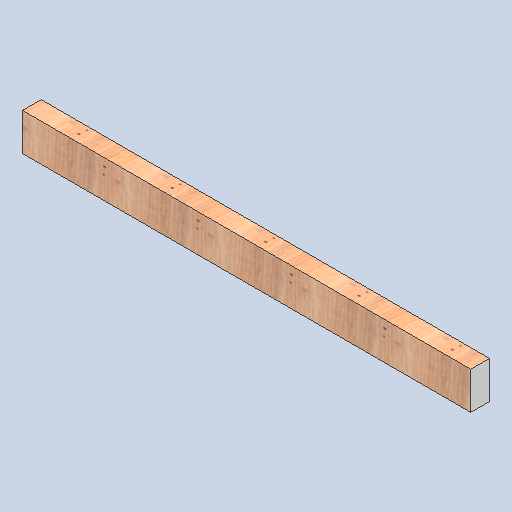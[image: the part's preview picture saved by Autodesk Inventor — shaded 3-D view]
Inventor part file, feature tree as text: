
AUTODESK INVENTOR PART (.ipt)
format: ipt  version: 2025 (Build 290162000, 162)  size: 326,144 bytes
history: native  units: in
note: dims shown in document units (in); Inventor stores cm internally (conversion verified against a paired STEP export)
features: extrude x2, sketch x2
ambient origin geometry x8: Origin, YZ Plane, XZ Plane, XY Plane, X Axis, Y Axis, Z Axis, Center Point
bodies: Solid1 (feature_tree)
feature tree (4):
  extrude  "Extrusion1"  Depth=4.0in
  extrude  "Extrusion2"  Depth=48.0in TaperAngle=0.0deg
  sketch  "Sketch1"  dims[d0=96.0in d1=4.0in]
  sketch  "Sketch2"  dims[d2=2.0in d3=0.0in d4=48.0in d5=0.0in]
